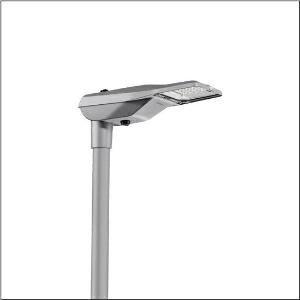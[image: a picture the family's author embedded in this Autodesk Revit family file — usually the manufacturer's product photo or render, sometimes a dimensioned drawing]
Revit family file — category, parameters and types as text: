
# Revit family: streetlight_sl_21_micro___st1_0a_5xe1d33t08db_ddb2
name_source: partatom
category: Lighting Fixtures
units: mm (PartAtom-declared; Revit-internal decimal feet)

## family parameters
Cut with Voids When Loaded = No
Host = Face
Light Source = No
Part Type = Normal
Room Calculation Point = No
Round Connector Dimension = Use Diameter
Shared = No

## types (1)
- --- (1 x LED, 5110 lm, 39.1 W, 3000K)
    Apparent Load = 39 VA
    CIE Flux Codes = 37 72 97 100 100
    Color Rendering = 70
    Color Temperature = 3000K
    Default Elevation = 1800 mm
    Description = Streetlight SL 21 micro, mast luminaire, primary light control with lens, of PMMA, primary optical cover: cover, of toughened safety glass, transparent, light distribution: ST1.0a, light emission: direct distribution, primary light characteristic: asymmetric, installation type: side-entry, post-top, LED, High Power LED, rated luminous flux: 5.110lm, luminous efficacy: 131lm/W, light colour: 730, colour temperature: 3000K, control gear: D4i, control: flexible luminous flux parameterisation, time-dependent luminous flux control, constant luminous flux control, overheat protection, pre-setting: logarithmic dimming characteristic, mains connection: 220..240V, AC, 50/60Hz, start of lifetime: 39W, end of service life: 41W, reduction: 18W, luminaire housing, of diecast aluminium, powder-coated, Siteco® metallic grey (DB 702S), corrosivity category C5 mid according to DIN EN ISO 12944, please order mast flange separately, inclination adjustable: 0°, 5°, 10°, 15°, sealing non-destructively replaceable, multi-level sealing system, length: 528mm, width: 235mm, height: 110mm, mast flange for spigot size: 42mm (side-entry): 5XC10008XM4, 60/48mm (side-entry/post-top): 5XC10108XM2, 76/60mm (side-entry/post-top): 5XC10108XM1, Smart Interface below and above, protection rating (complete): IP66, insulation class (complete): insulation class II (safety insulation), certification: CE, ENEC, ENEC+, VDE, impact resistance: IK09, permissible operating ambient temperature for outdoor applications: -40..+50°C, standard-compliant lighting for roads and squares, packaging unit: 1 piece

Light Distribution: ST1.0a
    Height = 110 mm
    Lamp = 1 x LED
    Lamp Light Flux = 5110 lm
    Lamp Power = 39.1 W
    Lamp count = 1
    Length = 528 mm
    Luminous efficacy = 131 lm/W
    Manufacturer = Siteco
    ModVariant = No
    Model = 5XE1D33T08DB
    Number of Poles = 1
    OnlyDefault = Yes
    Power Factor = 1
    Product Name = Streetlight SL 21 micro | ST1.0a
    Product group = mast luminaire | pylon top
    ProductGroupID = 6100
    Protection Class = Protection class II
    Protection Degree = IP 66
    RLX_Detail_Level = 1
    RLX_Emergency_Light_Flux = 0 lm
    RLX_Emergency_Type = 0
    RLX_Emergency_Type_DB = No
    RlxData = <blob elided: 98957 chars, md5=49a378af>
    Socket = socket
    Standby Power = 0 W
    System Light Flux = 5110 lm
    System Power = 39 W
    Type Comments = factory setting: luminous flux: 100 % | dim-lin: 254 | 765 mA
    Type Image = l_1007239.jpg
    URL = http://relux.com
    VarID = @adj_151428
    Voltage = 0 V
    Weight = 0.00 kg
    Width = 235 mm

## geometry (parser evidence)
native form markers: Blend x4, Sweep x10
no freeform markers — native parametric forms only
